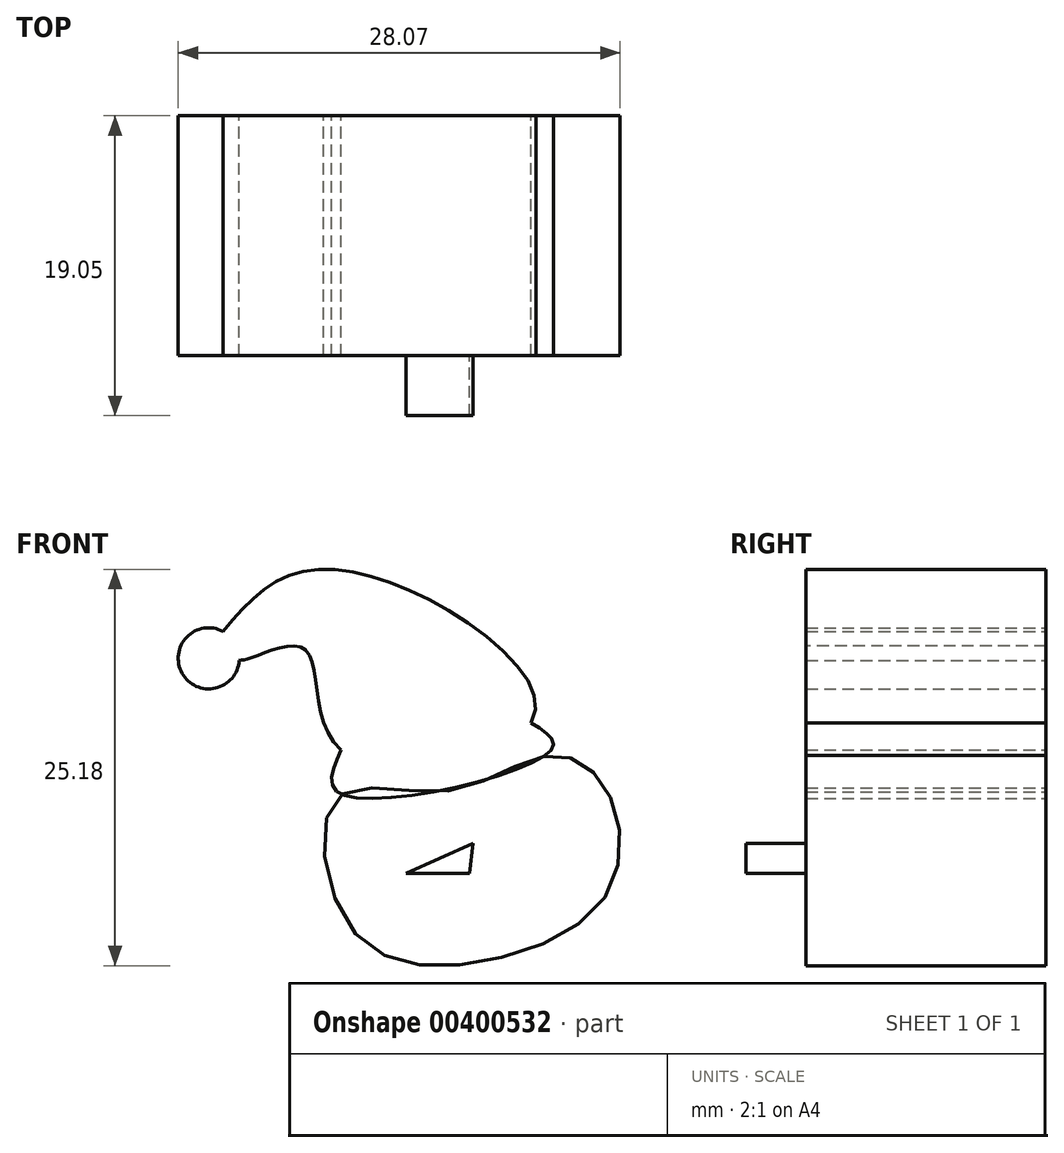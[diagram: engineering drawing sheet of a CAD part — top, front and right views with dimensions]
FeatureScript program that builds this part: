
annotation { "Feature Type Name" : "Feature", "Feature Type Description" : "" }
export const myFeature = defineFeature(function(context is Context, id is Id, definition is map)
    precondition{}
    {
        {
            var Q0;
            Q0=qCreatedBy(makeId("Front.planeOp"),FACE);
            var sketch = newSketch(context, id + "F0", { "sketchPlane" : qUnion([Q0])});
            skCircle(sketch, "E0", {"center": v(-42.12, 58.28) * mm, "radius": 3.23 * mm});
            skFitSpline(sketch, "E1", {"points": [v(-40.62, 61.14) * mm, v(-32.8, 67.34) * mm, v(-16.62, 63.26) * mm, v(-8, 51.45) * mm, v(-28.1, 48.6) * mm, v(-31.95, 59.23) * mm, v(-37.56, 58.36) * mm, v(-38.9, 58.06) * mm], "startDerivative": vector(48, 56.1) * mm, "endDerivative": vector(-17.69, -1.86) * mm});
            skFitSpline(sketch, "E2", {"points": [v(-28.1, 48.6) * mm, v(-28.1, 43.88) * mm, v(-5.84, 48.6) * mm, v(-8, 51.45) * mm], "startDerivative": vector(-10.63, -23.89) * mm, "endDerivative": vector(-20.7, 12.49) * mm});
            skSolve(sketch);
        }
        {
            var Q0;
            Q0=qCreatedBy(makeId("Front.planeOp"),FACE);
            var sketch = newSketch(context, id + "F1", { "sketchPlane" : qUnion([Q0])});
            skFitSpline(sketch, "E3", {"points": [v(-16.8, 44.26) * mm, v(-28.58, 43.44) * mm, v(-27.08, 29.76) * mm, v(-14.4, 26) * mm, v(0, 33.24) * mm, v(0, 44.32) * mm, v(-6, 48) * mm, v(-16.8, 44.26) * mm]});
            skSolve(sketch);
        }
        {
            var Q0;
            {var subQ0=sQuery(id+"F0.wireOp",EDGE,"E1");var subQ1=sQuery(id+"F0.wireOp",EDGE,"E0");var subQ2=makeQuery(id+"F0.imprint","INTERSECT",VERTEX,{"disambiguationData":[OD(0.0)],"derivedFrom":[subQ1,subQ0]});Q0=makeQuery(id+"F0.imprint","IMPRINT",FACE,{"disambiguationData":[TD([[makeQuery(id+"F0.imprint","IMPRINT",EDGE,{"disambiguationData":[TD([[subQ2,1.0]])],"derivedFrom":subQ1}),-1.0]])]});}
            var Q1;
            {var subQ0=sQuery(id+"F0.wireOp",EDGE,"E1");var subQ1=sQuery(id+"F0.wireOp",EDGE,"E0");var subQ2=makeQuery(id+"F0.imprint","INTERSECT",VERTEX,{"disambiguationData":[OD(0.0)],"derivedFrom":[subQ1,subQ0]});Q1=makeQuery(id+"F0.imprint","IMPRINT",FACE,{"disambiguationData":[TD([[makeQuery(id+"F0.imprint","IMPRINT",EDGE,{"disambiguationData":[TD([[subQ2,-1.0]])],"derivedFrom":subQ1}),1.0]])]});}
            var Q2;
            {var subQ0=sQuery(id+"F0.wireOp",EDGE,"E2");Q2=makeQuery(id+"F0.imprint","IMPRINT",FACE,{"disambiguationData":[TD([[makeQuery(id+"F0.imprint","IMPRINT",EDGE,{"derivedFrom":subQ0}),1.0]])]});}
            var Q3;
            Q3=makeQuery(id+"F1.imprint","IMPRINT",FACE,{"disambiguationData":[TD([[makeQuery(id+"F1.imprint","IMPRINT",EDGE,{"derivedFrom":sQuery(id+"F1.wireOp",EDGE,"E3")}),1.0]])]});
            extrude(context, id + "F2", {"entities" : qUnion([Q0, Q1, Q2, Q3]), "depth" : 25.4 * mm});
        }
        {
            var Q0;
            Q0=makeQuery(id+"F2.opExtrude","CAP_FACE",FACE,{"disambiguationData":[OSD([sQuery(id+"F1.wireOp",EDGE,"E3")])],"isStart":false});
            var sketch = newSketch(context, id + "F3", { "sketchPlane" : qUnion([Q0])});
            skLineSegment(sketch, "E4", {"start": v(-14.13, 38.68) * mm, "end": v(-21.25, 35.53) * mm});
            skLineSegment(sketch, "E5", {"start": v(-21.25, 35.53) * mm, "end": v(-14.5, 35.53) * mm});
            skLineSegment(sketch, "E6", {"start": v(-14.5, 35.53) * mm, "end": v(-14.13, 38.68) * mm});
            skSolve(sketch);
        }
        {
            var Q0;
            Q0=makeQuery(id+"F3.imprint","IMPRINT",FACE,{"disambiguationData":[TD([[makeQuery(id+"F3.imprint","IMPRINT",EDGE,{"derivedFrom":sQuery(id+"F3.wireOp",EDGE,"E4")}),1.0]])]});
            extrude(context, id + "F4", {"entities" : qUnion([Q0]), "operationType" : NewBodyOperationType.ADD, "depth" : 6.35 * mm});
        }
        {
            var Q0;
            Q0=makeQuery(id+"F2.opExtrude","SWEPT_BODY",BODY,{"disambiguationData":[OSD([sQuery(id+"F1.wireOp",EDGE,"E3")])]});
            var Q1;
            Q1=makeQuery(id+"F2.opExtrude","SWEPT_BODY",BODY,{"disambiguationData":[OSD([sQuery(id+"F0.wireOp",EDGE,"E0"),sQuery(id+"F0.wireOp",EDGE,"E1"),sQuery(id+"F0.wireOp",EDGE,"E2")])]});
            var Q2;
            Q2=qCreatedBy(makeId("Origin.pointOp"),VERTEX);
            transform(context, id + "F5", {"entities" : qUnion([Q0, Q1]), "transformType" : TransformType.SCALE_UNIFORMLY, "scale" : .6, "scalePoint" : qUnion([Q2]), "makeCopy" : false});
        }
    });
